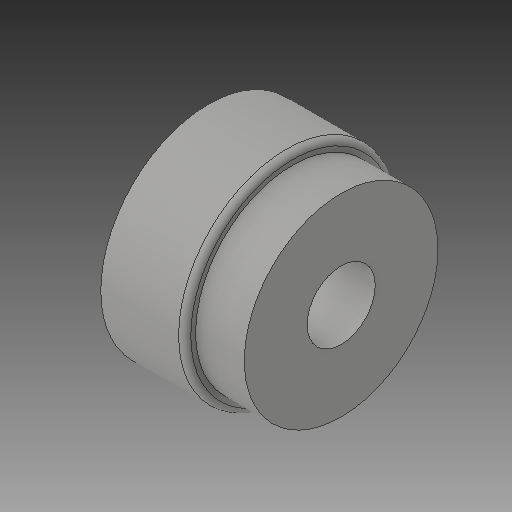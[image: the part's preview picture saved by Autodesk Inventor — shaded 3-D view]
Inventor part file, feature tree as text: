
AUTODESK INVENTOR PART (.ipt)
format: ipt  version: 2019 (Build 230136000, 136)  size: 148,992 bytes
history: native  units: mm
features: revolve x1, fillet x1, sketch x1
ambient origin geometry x8: Origin, YZ Plane, XZ Plane, XY Plane, X Axis, Y Axis, Z Axis, Center Point
bodies: Solid1 (feature_tree)
feature tree (3):
  revolve  "Revolution1"  [1 undecoded]
  fillet  "Fillet1"  Radius=17.72mm
  sketch  "Sketch1"  dims[d0=5.6mm d1=14.0mm d2=17.72mm d3=15.92mm d4=9.0mm d5=4.0mm d6=3.1mm d7=6.9mm d8=90.0deg d9=0.5mm]
note: 1 required parameter value undecoded (feature->parameter linkage not recoverable at this tier; creation-order binding heuristic only, values carry confidence <= 0.55)
